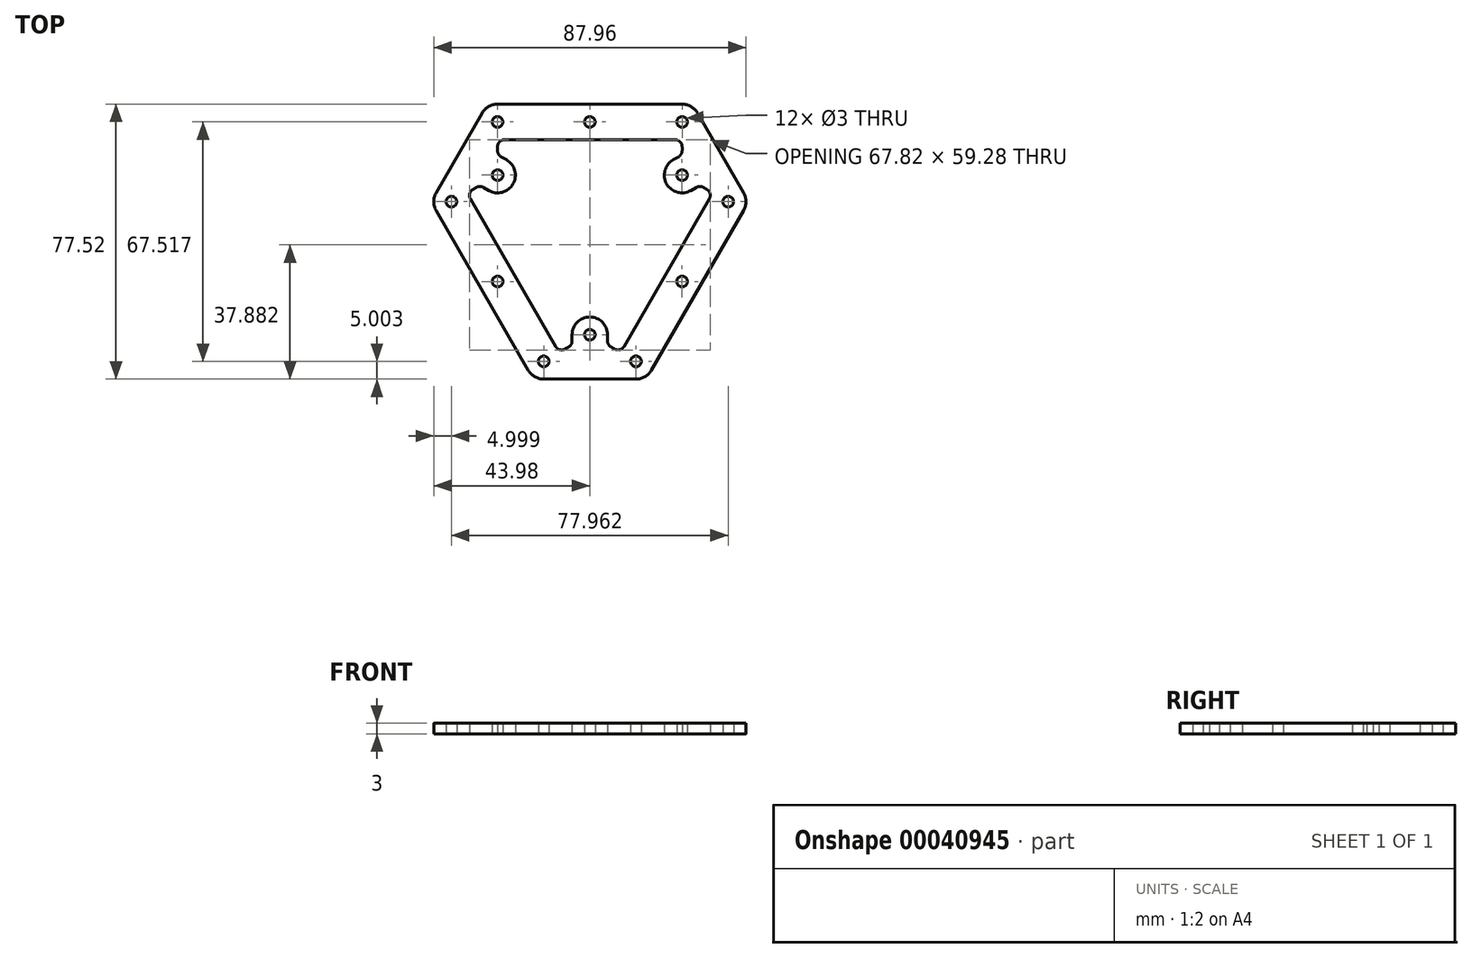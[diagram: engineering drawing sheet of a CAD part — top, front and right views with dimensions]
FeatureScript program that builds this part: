
annotation { "Feature Type Name" : "Feature", "Feature Type Description" : "" }
export const myFeature = defineFeature(function(context is Context, id is Id, definition is map)
    precondition{}
    {
        {
            var Q0;
            Q0=qCreatedBy(makeId("Top.planeOp"),FACE);
            var sketch = newSketch(context, id + "F0", { "sketchPlane" : qUnion([Q0])});
            skLineSegment(sketch, "E0", {"start": v(0, 0) * mm, "end": v(0, 30) * mm, "construction": true});
            skLineSegment(sketch, "E1", {"start": v(-26, 30) * mm, "end": v(26, 30) * mm, "construction": true});
            skLineSegment(sketch, "E2", {"start": v(0, 0) * mm, "end": v(25.98, -15) * mm, "construction": true});
            skLineSegment(sketch, "E3", {"start": v(0, 0) * mm, "end": v(-25.98, -15) * mm, "construction": true});
            skLineSegment(sketch, "E4", {"start": v(12.98, -37.52) * mm, "end": v(38.98, 7.52) * mm, "construction": true});
            skLineSegment(sketch, "E5", {"start": v(-12.98, -37.52) * mm, "end": v(-38.98, 7.52) * mm, "construction": true});
            skCircle(sketch, "E6", {"center": v(26, 30) * mm, "radius": 1.5 * mm});
            skCircle(sketch, "E7", {"center": v(0, 30) * mm, "radius": 1.5 * mm});
            skCircle(sketch, "E8", {"center": v(-26, 30) * mm, "radius": 1.5 * mm});
            skCircle(sketch, "E9", {"center": v(38.98, 7.52) * mm, "radius": 1.5 * mm});
            skCircle(sketch, "E10", {"center": v(25.98, -15) * mm, "radius": 1.5 * mm});
            skCircle(sketch, "E11", {"center": v(12.98, -37.52) * mm, "radius": 1.5 * mm});
            skCircle(sketch, "E12", {"center": v(-12.98, -37.52) * mm, "radius": 1.5 * mm});
            skCircle(sketch, "E13", {"center": v(-25.98, -15) * mm, "radius": 1.5 * mm});
            skCircle(sketch, "E14", {"center": v(-38.98, 7.52) * mm, "radius": 1.5 * mm});
            skLineSegment(sketch, "E15", {"start": v(0, 0) * mm, "end": v(-25.98, 15) * mm, "construction": true});
            skLineSegment(sketch, "E16", {"start": v(0, 0) * mm, "end": v(25.98, 15) * mm, "construction": true});
            skLineSegment(sketch, "E17", {"start": v(0, 0) * mm, "end": v(0, -30) * mm, "construction": true});
            skCircle(sketch, "E18", {"center": v(25.98, 15) * mm, "radius": 1.5 * mm});
            skCircle(sketch, "E19", {"center": v(-25.98, 15) * mm, "radius": 1.5 * mm});
            skCircle(sketch, "E20", {"center": v(0, -30) * mm, "radius": 1.5 * mm});
            skCircle(sketch, "E21", {"center": v(26, 30) * mm, "radius": 5 * mm});
            skCircle(sketch, "E22", {"center": v(-26, 30) * mm, "radius": 5 * mm});
            skCircle(sketch, "E23", {"center": v(-12.98, -37.52) * mm, "radius": 5 * mm});
            skCircle(sketch, "E24", {"center": v(-38.98, 7.52) * mm, "radius": 5 * mm});
            skCircle(sketch, "E25", {"center": v(12.98, -37.52) * mm, "radius": 5 * mm});
            skCircle(sketch, "E26", {"center": v(38.98, 7.52) * mm, "radius": 5 * mm});
            skLineSegment(sketch, "E27", {"start": v(30.33, 32.5) * mm, "end": v(43.31, 10.02) * mm});
            skLineSegment(sketch, "E28", {"start": v(43.31, 10.02) * mm, "end": v(38.98, 7.52) * mm, "construction": true});
            skLineSegment(sketch, "E29", {"start": v(30.33, 32.5) * mm, "end": v(26, 30) * mm, "construction": true});
            skLineSegment(sketch, "E30", {"start": v(-12.98, -37.52) * mm, "end": v(-12.98, -42.52) * mm, "construction": true});
            skLineSegment(sketch, "E31", {"start": v(-12.98, -42.52) * mm, "end": v(12.98, -42.52) * mm});
            skLineSegment(sketch, "E32", {"start": v(12.98, -42.52) * mm, "end": v(12.98, -37.52) * mm, "construction": true});
            skLineSegment(sketch, "E33", {"start": v(-26, 30) * mm, "end": v(-30.33, 32.5) * mm, "construction": true});
            skLineSegment(sketch, "E34", {"start": v(-30.33, 32.5) * mm, "end": v(-43.31, 10.02) * mm});
            skLineSegment(sketch, "E35", {"start": v(-43.31, 10.02) * mm, "end": v(-38.98, 7.52) * mm, "construction": true});
            skLineSegment(sketch, "E36", {"start": v(-26, 30) * mm, "end": v(-26, 35) * mm, "construction": true});
            skLineSegment(sketch, "E37", {"start": v(-26, 35) * mm, "end": v(26, 35) * mm});
            skLineSegment(sketch, "E38", {"start": v(26, 35) * mm, "end": v(26, 30) * mm, "construction": true});
            skLineSegment(sketch, "E39", {"start": v(12.98, -37.52) * mm, "end": v(17.31, -40.02) * mm, "construction": true});
            skLineSegment(sketch, "E40", {"start": v(17.31, -40.02) * mm, "end": v(43.31, 5.02) * mm});
            skLineSegment(sketch, "E41", {"start": v(43.31, 5.02) * mm, "end": v(38.98, 7.52) * mm, "construction": true});
            skLineSegment(sketch, "E42", {"start": v(-12.98, -37.52) * mm, "end": v(-17.31, -40.02) * mm, "construction": true});
            skLineSegment(sketch, "E43", {"start": v(-17.31, -40.02) * mm, "end": v(-43.31, 5.02) * mm});
            skLineSegment(sketch, "E44", {"start": v(-43.31, 5.02) * mm, "end": v(-38.98, 7.52) * mm, "construction": true});
            skLineSegment(sketch, "E45", {"start": v(38.98, 7.52) * mm, "end": v(34.65, 10.02) * mm, "construction": true});
            skLineSegment(sketch, "E46", {"start": v(33.65, 8.28) * mm, "end": v(9.65, -33.28) * mm});
            skLineSegment(sketch, "E47", {"start": v(8.65, -35.02) * mm, "end": v(12.98, -37.52) * mm, "construction": true});
            skLineSegment(sketch, "E48", {"start": v(26, 30) * mm, "end": v(26, 25) * mm, "construction": true});
            skLineSegment(sketch, "E49", {"start": v(24, 25) * mm, "end": v(-24, 25) * mm});
            skLineSegment(sketch, "E50", {"start": v(-26, 25) * mm, "end": v(-26, 30) * mm, "construction": true});
            skLineSegment(sketch, "E51", {"start": v(-38.98, 7.52) * mm, "end": v(-34.65, 10.02) * mm, "construction": true});
            skLineSegment(sketch, "E52", {"start": v(-33.65, 8.28) * mm, "end": v(-9.65, -33.28) * mm});
            skLineSegment(sketch, "E53", {"start": v(-8.65, -35.02) * mm, "end": v(-12.98, -37.52) * mm, "construction": true});
            skLineSegment(sketch, "E54", {"start": v(26, 23) * mm, "end": v(26, 21.93) * mm});
            skLineSegment(sketch, "E55", {"start": v(32.91, 11.02) * mm, "end": v(32, 11.55) * mm});
            skLineSegment(sketch, "E56", {"start": v(23.48, 19.33) * mm, "end": v(25, 20.2) * mm});
            skLineSegment(sketch, "E57", {"start": v(28.48, 10.67) * mm, "end": v(30, 11.54) * mm});
            skLineSegment(sketch, "E58", {"start": v(-6, -33.48) * mm, "end": v(-6.92, -34.01) * mm});
            skLineSegment(sketch, "E59", {"start": v(6.92, -34.01) * mm, "end": v(6, -33.48) * mm});
            skLineSegment(sketch, "E60", {"start": v(-32.91, 11.02) * mm, "end": v(-32, 11.55) * mm});
            skLineSegment(sketch, "E61", {"start": v(-26, 23) * mm, "end": v(-26, 21.93) * mm});
            skLineSegment(sketch, "E62", {"start": v(-5, -30) * mm, "end": v(-5, -31.75) * mm});
            skLineSegment(sketch, "E63", {"start": v(5, -30) * mm, "end": v(5, -31.75) * mm});
            skLineSegment(sketch, "E64", {"start": v(-23.48, 19.33) * mm, "end": v(-25, 20.2) * mm});
            skLineSegment(sketch, "E65", {"start": v(-28.48, 10.67) * mm, "end": v(-30, 11.54) * mm});
            skPoint(sketch, "E66.visualSharp", {"position": v(26, 25) * mm});
            skArc(sketch, "E66.filletArc", {"start": v(26, 23) * mm, "mid": v(25.41, 24.41) * mm, "end": v(24, 25) * mm});
            skArc(sketch, "E67.filletArc", {"start": v(25, 20.2) * mm, "mid": v(25.73, 20.93) * mm, "end": v(26, 21.93) * mm});
            skLineSegment(sketch, "E68", {"start": v(25.98, 15) * mm, "end": v(26, 25) * mm, "construction": true});
            skPoint(sketch, "E69.visualSharp", {"position": v(34.65, 10.02) * mm});
            skArc(sketch, "E69.filletArc", {"start": v(33.65, 8.28) * mm, "mid": v(33.85, 9.8) * mm, "end": v(32.91, 11.02) * mm});
            skArc(sketch, "E70.filletArc", {"start": v(32, 11.55) * mm, "mid": v(31, 11.81) * mm, "end": v(30, 11.54) * mm});
            skLineSegment(sketch, "E71", {"start": v(25.98, 15) * mm, "end": v(34.65, 10.02) * mm, "construction": true});
            skPoint(sketch, "E72.visualSharp", {"position": v(8.65, -35.02) * mm});
            skArc(sketch, "E72.filletArc", {"start": v(6.92, -34.01) * mm, "mid": v(8.44, -34.21) * mm, "end": v(9.65, -33.28) * mm});
            skArc(sketch, "E73.filletArc", {"start": v(5, -31.75) * mm, "mid": v(5.27, -32.75) * mm, "end": v(6, -33.48) * mm});
            skPoint(sketch, "E74.visualSharp", {"position": v(-8.65, -35.02) * mm});
            skArc(sketch, "E74.filletArc", {"start": v(-9.65, -33.28) * mm, "mid": v(-8.44, -34.21) * mm, "end": v(-6.92, -34.01) * mm});
            skArc(sketch, "E75.filletArc", {"start": v(-6, -33.48) * mm, "mid": v(-5.27, -32.75) * mm, "end": v(-5, -31.75) * mm});
            skLineSegment(sketch, "E76", {"start": v(-8.65, -35.02) * mm, "end": v(0, -30) * mm, "construction": true});
            skLineSegment(sketch, "E77", {"start": v(8.65, -35.02) * mm, "end": v(0, -30) * mm, "construction": true});
            skPoint(sketch, "E78.visualSharp", {"position": v(-26, 25) * mm});
            skArc(sketch, "E78.filletArc", {"start": v(-24, 25) * mm, "mid": v(-25.41, 24.41) * mm, "end": v(-26, 23) * mm});
            skArc(sketch, "E79.filletArc", {"start": v(-26, 21.93) * mm, "mid": v(-25.73, 20.93) * mm, "end": v(-25, 20.2) * mm});
            skPoint(sketch, "E80.visualSharp", {"position": v(-34.65, 10.02) * mm});
            skArc(sketch, "E80.filletArc", {"start": v(-32.91, 11.02) * mm, "mid": v(-33.85, 9.8) * mm, "end": v(-33.65, 8.28) * mm});
            skArc(sketch, "E81.filletArc", {"start": v(-30, 11.54) * mm, "mid": v(-31, 11.81) * mm, "end": v(-32, 11.55) * mm});
            skLineSegment(sketch, "E82", {"start": v(-25.98, 15) * mm, "end": v(-26, 25) * mm, "construction": true});
            skLineSegment(sketch, "E83", {"start": v(-34.65, 10.02) * mm, "end": v(-25.98, 15) * mm, "construction": true});
            skArc(sketch, "E84", {"start": v(23.48, 19.33) * mm, "mid": v(21.65, 12.5) * mm, "end": v(28.48, 10.67) * mm});
            skArc(sketch, "E85", {"start": v(28.48, 10.67) * mm, "mid": v(30.31, 17.5) * mm, "end": v(23.48, 19.33) * mm, "construction": true});
            skArc(sketch, "E86", {"start": v(-5, -30) * mm, "mid": v(0, -35) * mm, "end": v(5, -30) * mm, "construction": true});
            skArc(sketch, "E87", {"start": v(5, -30) * mm, "mid": v(0, -25) * mm, "end": v(-5, -30) * mm});
            skArc(sketch, "E88", {"start": v(-23.48, 19.33) * mm, "mid": v(-30.31, 17.5) * mm, "end": v(-28.48, 10.67) * mm, "construction": true});
            skArc(sketch, "E89", {"start": v(-28.48, 10.67) * mm, "mid": v(-21.65, 12.5) * mm, "end": v(-23.48, 19.33) * mm});
            skSolve(sketch);
        }
        {
            var Q0;
            Q0 = qSketchRegion(id + "F0", true);
            extrude(context, id + "F1", {"entities" : qUnion([Q0]), "depth" : 3 * mm});
        }
    });
